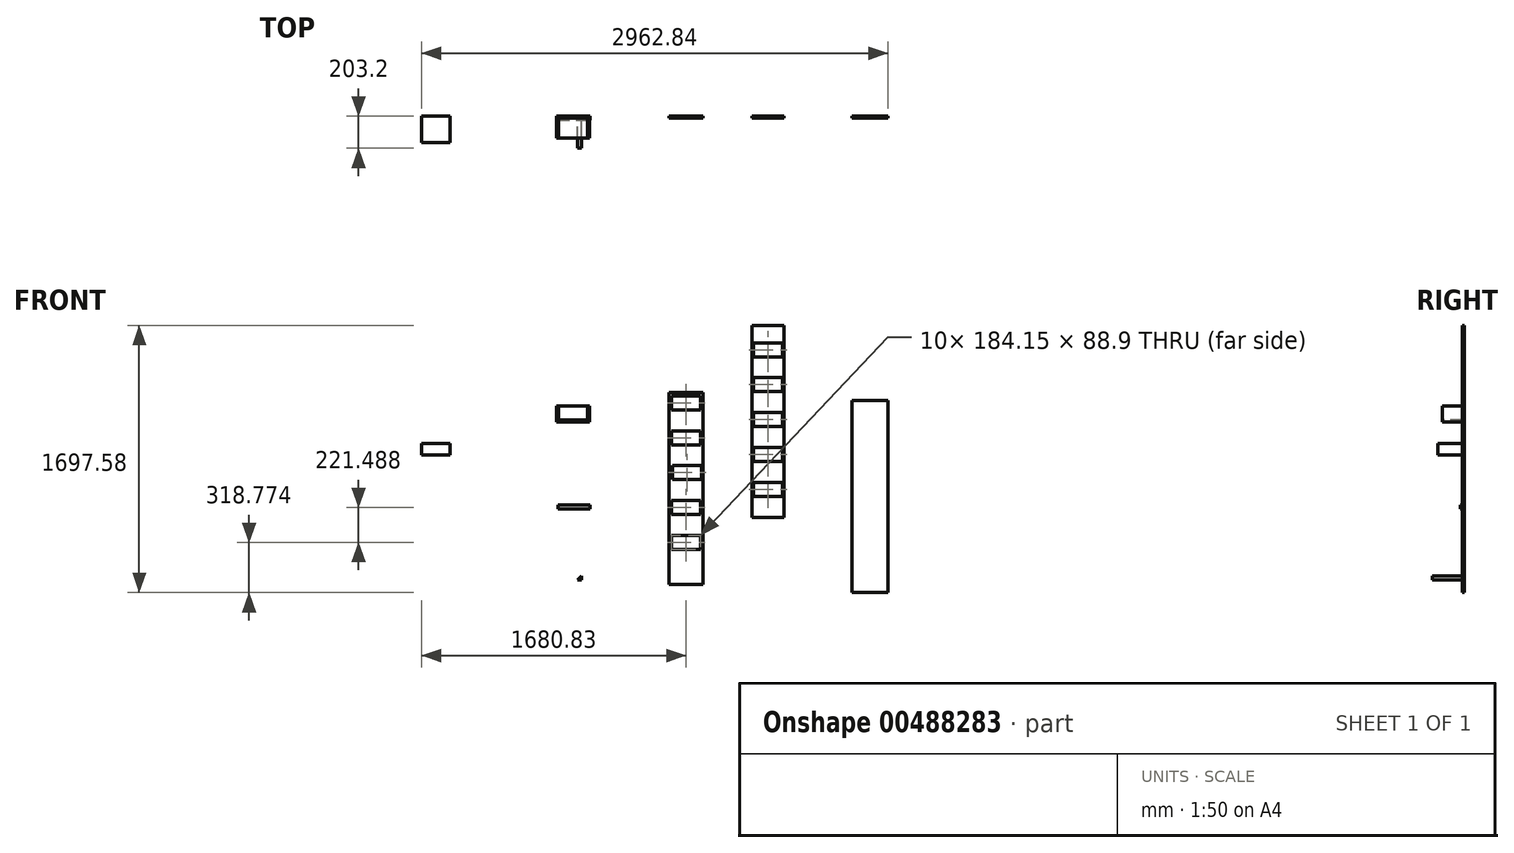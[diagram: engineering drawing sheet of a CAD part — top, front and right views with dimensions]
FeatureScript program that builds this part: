
annotation { "Feature Type Name" : "Feature", "Feature Type Description" : "" }
export const myFeature = defineFeature(function(context is Context, id is Id, definition is map)
    precondition{}
    {
        {
            var Q0;
            Q0=qCreatedBy(makeId("Front.planeOp"),FACE);
            var sketch = newSketch(context, id + "F0", { "sketchPlane" : qUnion([Q0])});
            skLineSegment(sketch, "E0.bottom", {"start": v(0, 0) * mm, "end": v(-215.9, 0) * mm});
            skLineSegment(sketch, "E0.top", {"start": v(0, 1219.2) * mm, "end": v(-215.9, 1219.2) * mm});
            skLineSegment(sketch, "E0.left", {"start": v(0, 0) * mm, "end": v(0, 1219.2) * mm});
            skLineSegment(sketch, "E0.right", {"start": v(-215.9, 0) * mm, "end": v(-215.9, 1219.2) * mm});
            skLineSegment(sketch, "E1.bottom", {"start": v(-200.03, 1197.36) * mm, "end": v(-15.88, 1197.36) * mm});
            skLineSegment(sketch, "E1.top", {"start": v(-200.03, 1108.46) * mm, "end": v(-15.88, 1108.46) * mm});
            skLineSegment(sketch, "E1.left", {"start": v(-200.03, 1197.36) * mm, "end": v(-200.03, 1108.46) * mm});
            skLineSegment(sketch, "E1.right", {"start": v(-15.88, 1197.36) * mm, "end": v(-15.88, 1108.46) * mm});
            skLineSegment(sketch, "E2.bottom", {"start": v(-200.03, 975.87) * mm, "end": v(-15.88, 975.87) * mm});
            skLineSegment(sketch, "E2.top", {"start": v(-200.03, 886.97) * mm, "end": v(-15.88, 886.97) * mm});
            skLineSegment(sketch, "E2.left", {"start": v(-200.03, 975.87) * mm, "end": v(-200.03, 886.97) * mm});
            skLineSegment(sketch, "E2.right", {"start": v(-15.88, 975.87) * mm, "end": v(-15.88, 886.97) * mm});
            skLineSegment(sketch, "E3.bottom", {"start": v(-193.67, 754.38) * mm, "end": v(-9.53, 754.38) * mm});
            skLineSegment(sketch, "E3.top", {"start": v(-193.67, 665.48) * mm, "end": v(-9.52, 665.48) * mm});
            skLineSegment(sketch, "E3.left", {"start": v(-193.67, 754.38) * mm, "end": v(-193.67, 665.48) * mm});
            skLineSegment(sketch, "E3.right", {"start": v(-9.53, 754.38) * mm, "end": v(-9.53, 665.48) * mm});
            skLineSegment(sketch, "E4.bottom", {"start": v(-200.03, 532.9) * mm, "end": v(-15.87, 532.9) * mm});
            skLineSegment(sketch, "E4.top", {"start": v(-200.03, 444) * mm, "end": v(-15.87, 444) * mm});
            skLineSegment(sketch, "E4.left", {"start": v(-200.03, 532.9) * mm, "end": v(-200.03, 444) * mm});
            skLineSegment(sketch, "E4.right", {"start": v(-15.87, 532.9) * mm, "end": v(-15.87, 444) * mm});
            skLineSegment(sketch, "E5.bottom", {"start": v(-200.03, 311.4) * mm, "end": v(-15.88, 311.4) * mm});
            skLineSegment(sketch, "E5.top", {"start": v(-200.03, 222.5) * mm, "end": v(-15.88, 222.5) * mm});
            skLineSegment(sketch, "E5.left", {"start": v(-200.03, 311.4) * mm, "end": v(-200.03, 222.5) * mm});
            skLineSegment(sketch, "E5.right", {"start": v(-15.88, 311.4) * mm, "end": v(-15.88, 222.5) * mm});
            skSolve(sketch);
        }
        {
            var Q0;
            Q0=makeQuery(id+"F0.imprint","IMPRINT",FACE,{"disambiguationData":[TD([[makeQuery(id+"F0.imprint","IMPRINT",EDGE,{"derivedFrom":sQuery(id+"F0.wireOp",EDGE,"E0.bottom")}),-1.0]])]});
            extrude(context, id + "F1", {"entities" : qUnion([Q0]), "depth" : 12.7 * mm});
        }
        {
            var Q0;
            Q0=qCreatedBy(makeId("Front.planeOp"),FACE);
            var sketch = newSketch(context, id + "F2", { "sketchPlane" : qUnion([Q0])});
            skLineSegment(sketch, "E6.bottom", {"start": v(310.08, 1645.76) * mm, "end": v(513.28, 1645.76) * mm});
            skLineSegment(sketch, "E6.top", {"start": v(310.08, 426.56) * mm, "end": v(513.28, 426.56) * mm});
            skLineSegment(sketch, "E6.left", {"start": v(310.08, 1645.76) * mm, "end": v(310.08, 426.56) * mm});
            skLineSegment(sketch, "E6.right", {"start": v(513.28, 1645.76) * mm, "end": v(513.28, 426.56) * mm});
            skLineSegment(sketch, "E7.bottom", {"start": v(319.6, 1535.02) * mm, "end": v(503.76, 1535.02) * mm});
            skLineSegment(sketch, "E7.top", {"start": v(319.6, 1446.12) * mm, "end": v(503.76, 1446.12) * mm});
            skLineSegment(sketch, "E7.left", {"start": v(319.6, 1535.02) * mm, "end": v(319.6, 1446.12) * mm});
            skLineSegment(sketch, "E7.right", {"start": v(503.76, 1535.02) * mm, "end": v(503.76, 1446.12) * mm});
            skLineSegment(sketch, "E8.bottom", {"start": v(319.6, 1313.53) * mm, "end": v(503.76, 1313.53) * mm});
            skLineSegment(sketch, "E8.top", {"start": v(319.6, 1224.63) * mm, "end": v(503.76, 1224.63) * mm});
            skLineSegment(sketch, "E8.left", {"start": v(319.6, 1313.53) * mm, "end": v(319.6, 1224.63) * mm});
            skLineSegment(sketch, "E8.right", {"start": v(503.76, 1313.53) * mm, "end": v(503.76, 1224.63) * mm});
            skLineSegment(sketch, "E9.top", {"start": v(319.6, 1003.14) * mm, "end": v(503.76, 1003.14) * mm});
            skLineSegment(sketch, "E9.left", {"start": v(319.6, 1092.04) * mm, "end": v(319.6, 1003.14) * mm});
            skLineSegment(sketch, "E9.right", {"start": v(503.76, 1092.04) * mm, "end": v(503.76, 1003.14) * mm});
            skLineSegment(sketch, "E10.bottom", {"start": v(319.6, 870.56) * mm, "end": v(503.76, 870.56) * mm});
            skLineSegment(sketch, "E10.top", {"start": v(319.6, 781.66) * mm, "end": v(503.76, 781.66) * mm});
            skLineSegment(sketch, "E10.left", {"start": v(319.6, 870.56) * mm, "end": v(319.6, 781.66) * mm});
            skLineSegment(sketch, "E10.right", {"start": v(503.76, 870.56) * mm, "end": v(503.76, 781.66) * mm});
            skLineSegment(sketch, "E11", {"start": v(319.6, 1092.04) * mm, "end": v(503.76, 1092.04) * mm});
            skLineSegment(sketch, "E12.bottom", {"start": v(319.6, 649.07) * mm, "end": v(503.76, 649.07) * mm});
            skLineSegment(sketch, "E12.top", {"start": v(319.6, 560.17) * mm, "end": v(503.76, 560.17) * mm});
            skLineSegment(sketch, "E12.left", {"start": v(319.6, 649.07) * mm, "end": v(319.6, 560.17) * mm});
            skLineSegment(sketch, "E12.right", {"start": v(503.76, 649.07) * mm, "end": v(503.76, 560.17) * mm});
            skSolve(sketch);
        }
        {
            var Q0;
            Q0=makeQuery(id+"F2.imprint","IMPRINT",FACE,{"disambiguationData":[TD([[makeQuery(id+"F2.imprint","IMPRINT",EDGE,{"derivedFrom":sQuery(id+"F2.wireOp",EDGE,"E6.bottom")}),-1.0]])]});
            extrude(context, id + "F3", {"entities" : qUnion([Q0]), "depth" : 12.7 * mm});
        }
        {
            var Q0;
            Q0=qCreatedBy(makeId("Front.planeOp"),FACE);
            var sketch = newSketch(context, id + "F4", { "sketchPlane" : qUnion([Q0])});
            skLineSegment(sketch, "E13.bottom", {"start": v(-930.56, 1132.5) * mm, "end": v(-721.01, 1132.5) * mm});
            skLineSegment(sketch, "E13.top", {"start": v(-930.56, 1030.9) * mm, "end": v(-721.01, 1030.9) * mm});
            skLineSegment(sketch, "E13.left", {"start": v(-930.56, 1132.5) * mm, "end": v(-930.56, 1030.9) * mm});
            skLineSegment(sketch, "E13.right", {"start": v(-721.01, 1132.5) * mm, "end": v(-721.01, 1030.9) * mm});
            skSolve(sketch);
        }
        {
            var Q0;
            Q0=makeQuery(id+"F4.imprint","IMPRINT",FACE,{"disambiguationData":[TD([[makeQuery(id+"F4.imprint","IMPRINT",EDGE,{"derivedFrom":sQuery(id+"F4.wireOp",EDGE,"E13.bottom")}),-1.0]])]});
            var Q1;
            Q1 = qSketchRegion(id + "F6", true);
            extrude(context, id + "F5", {"entities" : qUnion([Q0, Q1]), "depth" : 139.7 * mm});
        }
        {
            var Q0;
            Q0=makeQuery(id+"F5.opExtrude","SWEPT_FACE",FACE,{"disambiguationData":[OSD([sQuery(id+"F4.wireOp",EDGE,"E13.bottom")])]});
            var sketch = newSketch(context, id + "F6", { "sketchPlane" : qUnion([Q0])});
            skLineSegment(sketch, "E14.bottom", {"start": v(-917.86, -12.7) * mm, "end": v(-733.71, -12.7) * mm});
            skLineSegment(sketch, "E14.top", {"start": v(-917.86, -139.7) * mm, "end": v(-733.71, -139.7) * mm});
            skLineSegment(sketch, "E14.left", {"start": v(-917.86, -12.7) * mm, "end": v(-917.86, -139.7) * mm});
            skLineSegment(sketch, "E14.right", {"start": v(-733.71, -12.7) * mm, "end": v(-733.71, -139.7) * mm});
            skSolve(sketch);
        }
        {
            var Q0;
            Q0=makeQuery(id+"F6.imprint","IMPRINT",FACE,{"disambiguationData":[TD([[makeQuery(id+"F6.imprint","IMPRINT",EDGE,{"derivedFrom":sQuery(id+"F6.wireOp",EDGE,"E14.bottom")}),-1.0]])]});
            extrude(context, id + "F7", {"entities" : qUnion([Q0]), "operationType" : NewBodyOperationType.REMOVE, "oppositeDirection" : true, "depth" : 88.9 * mm});
        }
        {
            var Q0;
            Q0=qCreatedBy(makeId("Front.planeOp"),FACE);
            var sketch = newSketch(context, id + "F8", { "sketchPlane" : qUnion([Q0])});
            skLineSegment(sketch, "E15.bottom", {"start": v(-922.44, 506.66) * mm, "end": v(-719.24, 506.66) * mm});
            skLineSegment(sketch, "E15.top", {"start": v(-922.44, 481.26) * mm, "end": v(-719.24, 481.26) * mm});
            skLineSegment(sketch, "E15.left", {"start": v(-922.44, 506.66) * mm, "end": v(-922.44, 481.26) * mm});
            skLineSegment(sketch, "E15.right", {"start": v(-719.24, 506.66) * mm, "end": v(-719.24, 481.26) * mm});
            skSolve(sketch);
        }
        {
            var Q0;
            Q0=qCreatedBy(makeId("Front.planeOp"),FACE);
            var sketch = newSketch(context, id + "F9", { "sketchPlane" : qUnion([Q0])});
            skLineSegment(sketch, "E16.bottom", {"start": v(-1788.78, 896.63) * mm, "end": v(-1607.8, 896.63) * mm});
            skLineSegment(sketch, "E16.top", {"start": v(-1788.78, 823.6) * mm, "end": v(-1607.8, 823.6) * mm});
            skLineSegment(sketch, "E16.left", {"start": v(-1788.78, 896.63) * mm, "end": v(-1788.78, 823.6) * mm});
            skLineSegment(sketch, "E16.right", {"start": v(-1607.8, 896.63) * mm, "end": v(-1607.8, 823.6) * mm});
            skSolve(sketch);
        }
        {
            var Q0;
            Q0=makeQuery(id+"F8.imprint","IMPRINT",FACE,{"disambiguationData":[TD([[makeQuery(id+"F8.imprint","IMPRINT",EDGE,{"derivedFrom":sQuery(id+"F8.wireOp",EDGE,"E15.bottom")}),-1.0]])]});
            extrude(context, id + "F10", {"entities" : qUnion([Q0]), "depth" : 25.4 * mm});
        }
        {
            var Q0;
            Q0=makeQuery(id+"F9.imprint","IMPRINT",FACE,{"disambiguationData":[TD([[makeQuery(id+"F9.imprint","IMPRINT",EDGE,{"derivedFrom":sQuery(id+"F9.wireOp",EDGE,"E16.bottom")}),-1.0]])]});
            extrude(context, id + "F11", {"entities" : qUnion([Q0]), "depth" : 168.27 * mm});
        }
        {
            var Q0;
            Q0=qCreatedBy(makeId("Front.planeOp"),FACE);
            var sketch = newSketch(context, id + "F12", { "sketchPlane" : qUnion([Q0])});
            skLineSegment(sketch, "E17.bottom", {"start": v(945.46, 1167.38) * mm, "end": v(1174.06, 1167.38) * mm});
            skLineSegment(sketch, "E17.top", {"start": v(945.46, -51.82) * mm, "end": v(1174.06, -51.82) * mm});
            skLineSegment(sketch, "E17.left", {"start": v(945.46, 1167.38) * mm, "end": v(945.46, -51.82) * mm});
            skLineSegment(sketch, "E17.right", {"start": v(1174.06, 1167.38) * mm, "end": v(1174.06, -51.82) * mm});
            skSolve(sketch);
        }
        {
            var Q0;
            Q0=makeQuery(id+"F12.imprint","IMPRINT",FACE,{"disambiguationData":[TD([[makeQuery(id+"F12.imprint","IMPRINT",EDGE,{"derivedFrom":sQuery(id+"F12.wireOp",EDGE,"E17.bottom")}),-1.0]])]});
            extrude(context, id + "F13", {"entities" : qUnion([Q0]), "depth" : 12.7 * mm});
        }
        {
            var Q0;
            Q0=qCreatedBy(makeId("Front.planeOp"),FACE);
            var sketch = newSketch(context, id + "F14", { "sketchPlane" : qUnion([Q0])});
            skLineSegment(sketch, "E18", {"start": v(-771.36, 55.69) * mm, "end": v(-771.36, 30.29) * mm});
            skLineSegment(sketch, "E19", {"start": v(-771.36, 30.29) * mm, "end": v(-796.76, 30.29) * mm});
            skLineSegment(sketch, "E20", {"start": v(-796.76, 30.29) * mm, "end": v(-771.36, 55.69) * mm});
            skSolve(sketch);
        }
        {
            var Q0;
            Q0=makeQuery(id+"F14.imprint","IMPRINT",FACE,{"disambiguationData":[TD([[makeQuery(id+"F14.imprint","IMPRINT",EDGE,{"derivedFrom":sQuery(id+"F14.wireOp",EDGE,"E18")}),-1.0]])]});
            extrude(context, id + "F15", {"entities" : qUnion([Q0]), "depth" : 203.2 * mm});
        }
    });
